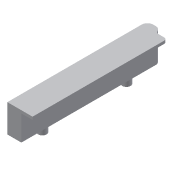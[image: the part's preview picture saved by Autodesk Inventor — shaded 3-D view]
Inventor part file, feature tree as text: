
AUTODESK INVENTOR PART (.ipt)
format: ipt  version: 2013 (Build 170138000, 138)  size: 102,400 bytes
history: native  units: mm
features: extrude x3, sketch x3, fillet x1
ambient origin geometry x8: Origin, YZ Plane, XZ Plane, XY Plane, X Axis, Y Axis, Z Axis, Center Point
bodies: Volumenkörper1 (feature_tree)
feature tree (7):
  extrude  "Extrusion1"  Depth=50.0mm
  extrude  "Extrusion2"  Depth=10.0mm TaperAngle=0.0deg
  fillet  "Rundung1"  Radius=1.0mm
  extrude  "Extrusion3"  Depth=1.0mm
  sketch  "Skizze1"  dims[d0=5.0mm d1=50.0mm]
  sketch  "Skizze2"  dims[d2=2.0mm d3=10.0mm d4=0.0mm d5=1.0mm]
  sketch  "Skizze3"  dims[d6=4.0mm d7=0.0mm d8=1.0mm d9=3.0mm d10=3.0mm d11=2.5mm d12=2.5mm d13=10.0mm d14=40.0mm d15=3.0mm d16=0.0mm]
